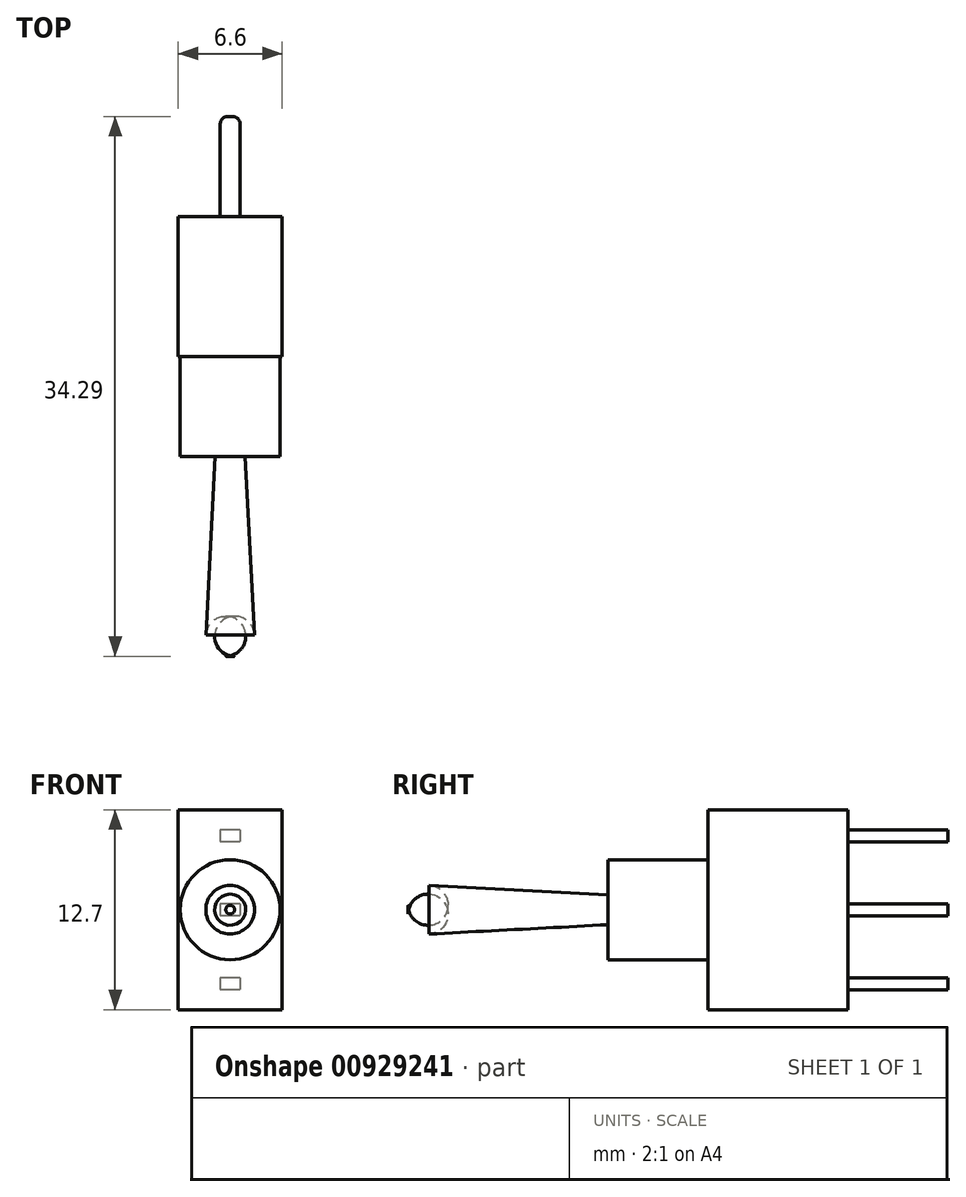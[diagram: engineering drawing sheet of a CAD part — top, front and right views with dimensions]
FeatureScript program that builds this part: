
annotation { "Feature Type Name" : "Feature", "Feature Type Description" : "" }
export const myFeature = defineFeature(function(context is Context, id is Id, definition is map)
    precondition{}
    {
        {
            var Q0;
            Q0=qCreatedBy(makeId("Front.planeOp"),FACE);
            var sketch = newSketch(context, id + "F0", { "sketchPlane" : qUnion([Q0])});
            skLineSegment(sketch, "E0.bottom", {"start": v(-3.3, 6.35) * mm, "end": v(3.3, 6.35) * mm});
            skLineSegment(sketch, "E0.top", {"start": v(-3.3, -6.35) * mm, "end": v(3.3, -6.35) * mm});
            skLineSegment(sketch, "E0.left", {"start": v(-3.3, 6.35) * mm, "end": v(-3.3, -6.35) * mm});
            skLineSegment(sketch, "E0.right", {"start": v(3.3, 6.35) * mm, "end": v(3.3, -6.35) * mm});
            skPoint(sketch, "E0.middle", {"position": v(0, 0) * mm});
            skCircle(sketch, "E1", {"center": v(0, 0) * mm, "radius": 3.18 * mm});
            skSolve(sketch);
        }
        {
            var Q0;
            Q0=makeQuery(id+"F0.imprint","IMPRINT",FACE,{"disambiguationData":[TD([[makeQuery(id+"F0.imprint","IMPRINT",EDGE,{"derivedFrom":sQuery(id+"F0.wireOp",EDGE,"E0.bottom")}),-1.0]])]});
            var Q1;
            Q1=makeQuery(id+"F0.imprint","IMPRINT",FACE,{"disambiguationData":[TD([[makeQuery(id+"F0.imprint","IMPRINT",EDGE,{"derivedFrom":sQuery(id+"F0.wireOp",EDGE,"E1")}),1.0]])]});
            extrude(context, id + "F1", {"entities" : qUnion([Q0, Q1]), "oppositeDirection" : true, "depth" : 8.9 * mm, "offsetDistance" : 25.4 * mm});
        }
        {
            var Q0;
            Q0=makeQuery(id+"F0.imprint","IMPRINT",FACE,{"disambiguationData":[TD([[makeQuery(id+"F0.imprint","IMPRINT",EDGE,{"derivedFrom":sQuery(id+"F0.wireOp",EDGE,"E1")}),1.0]])]});
            extrude(context, id + "F2", {"entities" : qUnion([Q0]), "operationType" : NewBodyOperationType.ADD, "depth" : 6.35 * mm, "offsetDistance" : 25.4 * mm});
        }
        {
            var Q0;
            Q0=makeQuery(id+"F2.opExtrude","CAP_FACE",FACE,{"disambiguationData":[OSD([sQuery(id+"F0.wireOp",EDGE,"E1")])],"isStart":false});
            var sketch = newSketch(context, id + "F3", { "sketchPlane" : qUnion([Q0])});
            skCircle(sketch, "E2", {"center": v(0, 0) * mm, "radius": 0.95 * mm});
            skSolve(sketch);
        }
        {
            var Q0;
            Q0=makeQuery(id+"F3.imprint","IMPRINT",FACE,{"disambiguationData":[TD([[makeQuery(id+"F3.imprint","IMPRINT",EDGE,{"derivedFrom":sQuery(id+"F3.wireOp",EDGE,"E2")}),1.0]])]});
            extrude(context, id + "F4", {"entities" : qUnion([Q0]), "operationType" : NewBodyOperationType.ADD, "depth" : 12.7 * mm, "offsetDistance" : 25.4 * mm, "hasDraft" : true, "draftAngle" : 3 * degree});
        }
        {
            var Q0;
            Q0=makeQuery(id+"F4.opExtrude","CAP_EDGE",EDGE,{"disambiguationData":[OSD([sQuery(id+"F3.wireOp",EDGE,"E2")])],"isStart":false});
            fillet(context, id + "F5", {"entities" : qUnion([Q0]), "tangentPropagation" : true, "radius" : 1.27 * mm, "defaultsChanged" : true, "vertexSettings" : [], "allowEdgeOverflow" : false});
        }
        {
            var Q0;
            Q0=makeQuery(id+"F1.opExtrude","CAP_FACE",FACE,{"disambiguationData":[OSD([sQuery(id+"F0.wireOp",EDGE,"E0.bottom"),sQuery(id+"F0.wireOp",EDGE,"E0.top"),sQuery(id+"F0.wireOp",EDGE,"E0.left"),sQuery(id+"F0.wireOp",EDGE,"E0.right")])],"isStart":false});
            var sketch = newSketch(context, id + "F6", { "sketchPlane" : qUnion([Q0])});
            skLineSegment(sketch, "E3.bottom", {"start": v(-0.64, 5.08) * mm, "end": v(0.64, 5.08) * mm});
            skLineSegment(sketch, "E3.top", {"start": v(-0.63, 4.32) * mm, "end": v(0.64, 4.32) * mm});
            skLineSegment(sketch, "E3.left", {"start": v(-0.63, 5.08) * mm, "end": v(-0.63, 4.32) * mm});
            skLineSegment(sketch, "E3.right", {"start": v(0.64, 5.08) * mm, "end": v(0.64, 4.32) * mm});
            skLineSegment(sketch, "E4.0.1.0", {"start": v(-0.64, 0.38) * mm, "end": v(0.64, 0.38) * mm});
            skLineSegment(sketch, "E4.0.1.1", {"start": v(-0.63, 0.38) * mm, "end": v(-0.63, -0.38) * mm});
            skLineSegment(sketch, "E4.0.1.2", {"start": v(0.64, 0.38) * mm, "end": v(0.64, -0.38) * mm});
            skLineSegment(sketch, "E4.0.1.3", {"start": v(-0.63, -0.38) * mm, "end": v(0.64, -0.38) * mm});
            skLineSegment(sketch, "E4.0.2.0", {"start": v(-0.64, -4.32) * mm, "end": v(0.64, -4.32) * mm});
            skLineSegment(sketch, "E4.0.2.1", {"start": v(-0.63, -4.32) * mm, "end": v(-0.63, -5.08) * mm});
            skLineSegment(sketch, "E4.0.2.2", {"start": v(0.64, -4.32) * mm, "end": v(0.64, -5.08) * mm});
            skLineSegment(sketch, "E4.0.2.3", {"start": v(-0.63, -5.08) * mm, "end": v(0.64, -5.08) * mm});
            skLineSegment(sketch, "E4.direction1", {"start": v(-0.64, 5.08) * mm, "end": v(1.55, 5.08) * mm, "construction": true});
            skLineSegment(sketch, "E4.direction2", {"start": v(-0.64, 5.08) * mm, "end": v(-0.64, 0.38) * mm, "construction": true});
            skSolve(sketch);
        }
        {
            var Q0;
            Q0 = qSketchRegion(id + "F6", true);
            extrude(context, id + "F7", {"entities" : qUnion([Q0]), "operationType" : NewBodyOperationType.ADD, "depth" : 6.35 * mm, "offsetDistance" : 25.4 * mm});
        }
        {
            var Q0;
            Q0=makeQuery(id+"F7.opExtrude","CAP_EDGE",EDGE,{"disambiguationData":[OSD([sQuery(id+"F6.wireOp",EDGE,"E3.left")])],"isStart":false});
            var Q1;
            Q1=makeQuery(id+"F7.opExtrude","CAP_EDGE",EDGE,{"disambiguationData":[OSD([sQuery(id+"F6.wireOp",EDGE,"E3.right")])],"isStart":false});
            var Q2;
            Q2=makeQuery(id+"F7.opExtrude","CAP_EDGE",EDGE,{"disambiguationData":[OSD([sQuery(id+"F6.wireOp",EDGE,"E4.0.1.1")])],"isStart":false});
            var Q3;
            Q3=makeQuery(id+"F7.opExtrude","CAP_EDGE",EDGE,{"disambiguationData":[OSD([sQuery(id+"F6.wireOp",EDGE,"E4.0.1.2")])],"isStart":false});
            var Q4;
            Q4=makeQuery(id+"F7.opExtrude","CAP_EDGE",EDGE,{"disambiguationData":[OSD([sQuery(id+"F6.wireOp",EDGE,"E4.0.2.1")])],"isStart":false});
            var Q5;
            Q5=makeQuery(id+"F7.opExtrude","CAP_EDGE",EDGE,{"disambiguationData":[OSD([sQuery(id+"F6.wireOp",EDGE,"E4.0.2.2")])],"isStart":false});
            fillet(context, id + "F8", {"entities" : qUnion([Q0, Q1, Q2, Q3, Q4, Q5]), "tangentPropagation" : true, "radius" : 0.5 * mm, "defaultsChanged" : true, "vertexSettings" : [], "allowEdgeOverflow" : false});
        }
    });
